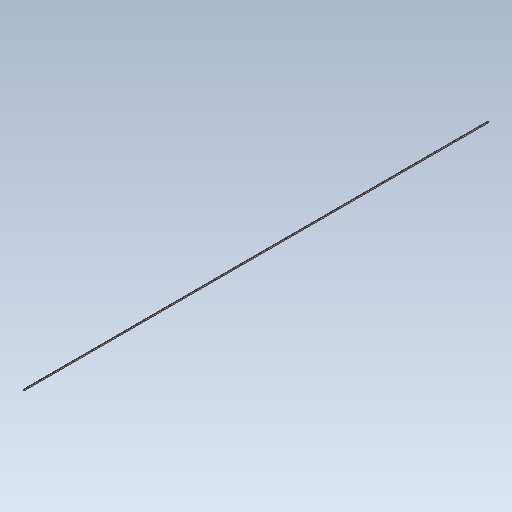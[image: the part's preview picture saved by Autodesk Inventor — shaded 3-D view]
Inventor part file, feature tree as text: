
AUTODESK INVENTOR PART (.ipt)
format: ipt  version: 2020.1 (Build 241239000, 239)  size: 98,304 bytes
history: native  units: mm
features: extrude x1, sketch x1
ambient origin geometry x8: Origin, YZ Plane, XZ Plane, XY Plane, X Axis, Y Axis, Z Axis, Center Point
bodies: Solid1 (feature_tree)
feature tree (2):
  extrude  "Extrusion1"  Depth=12.0mm
  sketch  "Sketch1"  dims[d0=6.0mm d1=12.0mm d2=4830.551mm d3=0.0mm]
